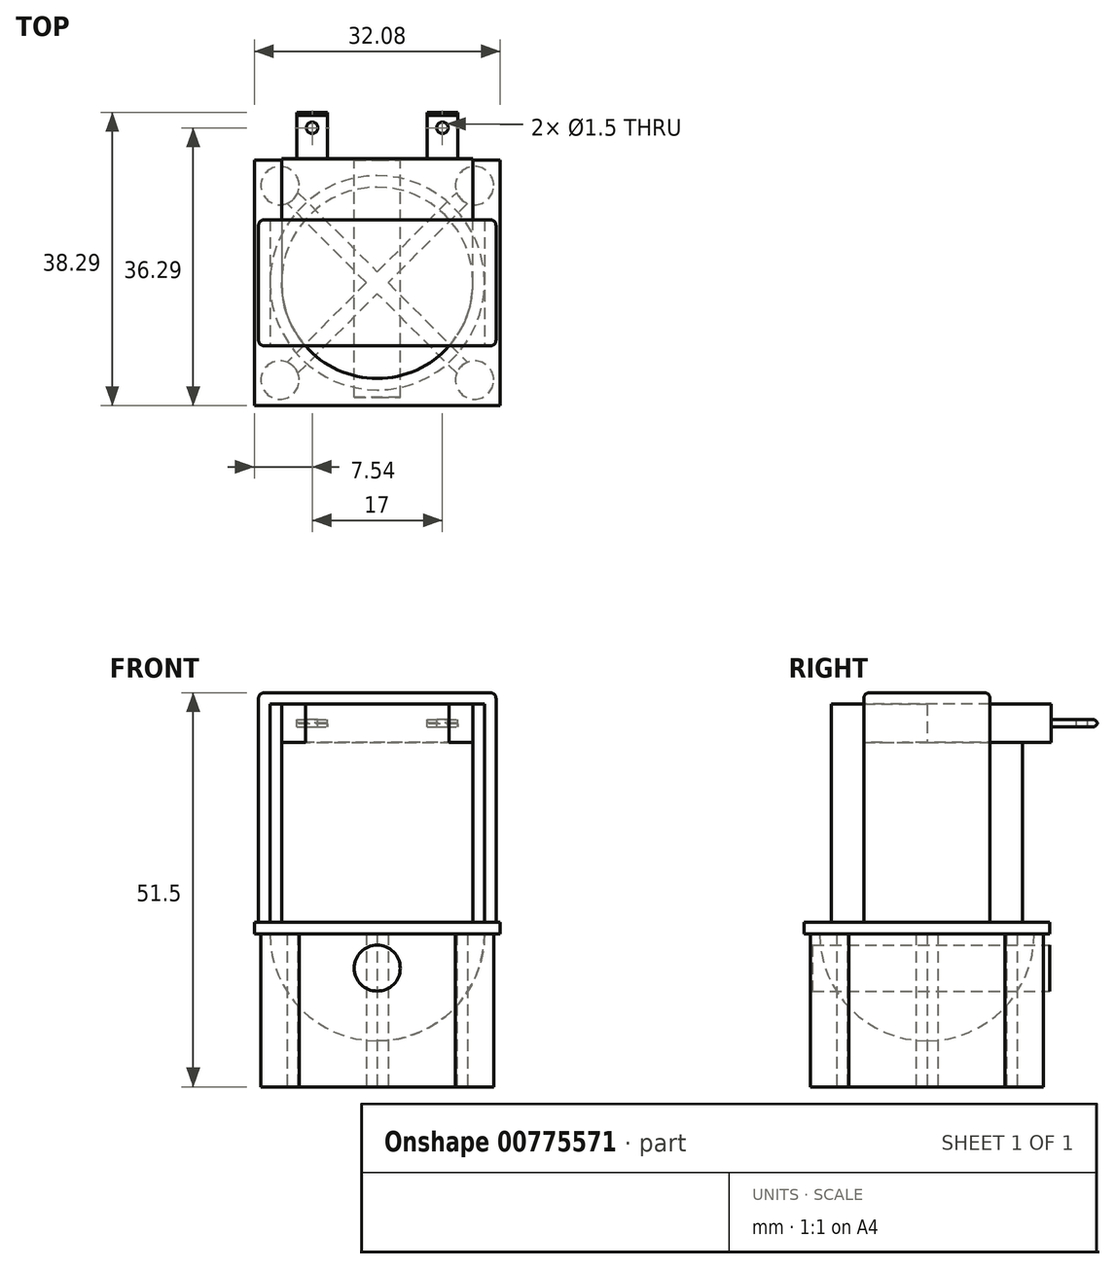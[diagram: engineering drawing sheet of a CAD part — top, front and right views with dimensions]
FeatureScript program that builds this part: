
annotation { "Feature Type Name" : "Feature", "Feature Type Description" : "" }
export const myFeature = defineFeature(function(context is Context, id is Id, definition is map)
    precondition{}
    {
        {
            var Q0;
            Q0=qCreatedBy(makeId("Top.planeOp"),FACE);
            var sketch = newSketch(context, id + "F0", { "sketchPlane" : qUnion([Q0])});
            skLineSegment(sketch, "E0.bottom", {"start": v(15.5, -8.25) * mm, "end": v(-15.5, -8.25) * mm});
            skLineSegment(sketch, "E0.top", {"start": v(15.5, 8.25) * mm, "end": v(-15.5, 8.25) * mm});
            skLineSegment(sketch, "E0.left", {"start": v(15.5, -8.25) * mm, "end": v(15.5, 8.25) * mm});
            skLineSegment(sketch, "E0.right", {"start": v(-15.5, -8.25) * mm, "end": v(-15.5, 8.25) * mm});
            skPoint(sketch, "E0.middle", {"position": v(0, 0) * mm});
            skSolve(sketch);
        }
        {
            var Q0;
            Q0 = qSketchRegion(id + "F0", true);
            extrude(context, id + "F1", {"entities" : qUnion([Q0]), "depth" : 30 * mm, "offsetDistance" : 25.4 * mm});
        }
        {
            var Q0;
            Q0=makeQuery(id+"F1.opExtrude","SWEPT_FACE",FACE,{"disambiguationData":[OSD([sQuery(id+"F0.wireOp",EDGE,"E0.bottom")])]});
            var sketch = newSketch(context, id + "F2", { "sketchPlane" : qUnion([Q0])});
            skLineSegment(sketch, "E1.bottom", {"start": v(-14, 0) * mm, "end": v(14, 0) * mm});
            skLineSegment(sketch, "E1.top", {"start": v(-14, 28.5) * mm, "end": v(14, 28.5) * mm});
            skLineSegment(sketch, "E1.left", {"start": v(-14, 0) * mm, "end": v(-14, 28.5) * mm});
            skLineSegment(sketch, "E1.right", {"start": v(14, 0) * mm, "end": v(14, 28.5) * mm});
            skSolve(sketch);
        }
        {
            var Q0;
            Q0 = qSketchRegion(id + "F2", true);
            extrude(context, id + "F3", {"entities" : qUnion([Q0]), "operationType" : NewBodyOperationType.REMOVE, "endBound" : BoundingType.UP_TO_NEXT, "oppositeDirection" : true, "depth" : 25.4 * mm, "offsetDistance" : 25.4 * mm});
        }
        {
            var Q0;
            Q0=makeQuery(id+"F1.opExtrude","SWEPT_EDGE",EDGE,{"disambiguationData":[OSD([sQuery(id+"F0.wireOp",EDGE,"E0.top"),sQuery(id+"F0.wireOp",EDGE,"E0.left")])]});
            var Q1;
            Q1=makeQuery(id+"F1.opExtrude","CAP_EDGE",EDGE,{"disambiguationData":[OSD([sQuery(id+"F0.wireOp",EDGE,"E0.top")])],"isStart":false});
            var Q2;
            Q2=makeQuery(id+"F1.opExtrude","SWEPT_EDGE",EDGE,{"disambiguationData":[OSD([sQuery(id+"F0.wireOp",EDGE,"E0.top"),sQuery(id+"F0.wireOp",EDGE,"E0.right")])]});
            var Q3;
            Q3=makeQuery(id+"F1.opExtrude","CAP_EDGE",EDGE,{"disambiguationData":[OSD([sQuery(id+"F0.wireOp",EDGE,"E0.left")])],"isStart":false});
            var Q4;
            Q4=makeQuery(id+"F1.opExtrude","SWEPT_EDGE",EDGE,{"disambiguationData":[OSD([sQuery(id+"F0.wireOp",EDGE,"E0.bottom"),sQuery(id+"F0.wireOp",EDGE,"E0.left")])]});
            var Q5;
            Q5=makeQuery(id+"F1.opExtrude","CAP_EDGE",EDGE,{"disambiguationData":[OSD([sQuery(id+"F0.wireOp",EDGE,"E0.bottom")])],"isStart":false});
            var Q6;
            Q6=makeQuery(id+"F1.opExtrude","CAP_EDGE",EDGE,{"disambiguationData":[OSD([sQuery(id+"F0.wireOp",EDGE,"E0.right")])],"isStart":false});
            var Q7;
            Q7=makeQuery(id+"F1.opExtrude","SWEPT_EDGE",EDGE,{"disambiguationData":[OSD([sQuery(id+"F0.wireOp",EDGE,"E0.bottom"),sQuery(id+"F0.wireOp",EDGE,"E0.right")])]});
            fillet(context, id + "F4", {"entities" : qUnion([Q0, Q1, Q2, Q3, Q4, Q5, Q6, Q7]), "radius" : 0.76 * mm, "tangentPropagation" : true, "allowEdgeOverflow" : false});
        }
        {
            var Q0;
            Q0=makeQuery(id+"F3.boolean.opBoolean","COPY",FACE,{"derivedFrom":makeQuery(id+"F3.opExtrude","SWEPT_FACE",FACE,{"disambiguationData":[OSD([sQuery(id+"F2.wireOp",EDGE,"E1.top")])]})});
            var sketch = newSketch(context, id + "F5", { "sketchPlane" : qUnion([Q0])});
            skLineSegment(sketch, "E2.bottom", {"start": v(14, -16.25) * mm, "end": v(-14, -16.25) * mm});
            skLineSegment(sketch, "E2.top", {"start": v(14, 8.25) * mm, "end": v(-14, 8.25) * mm});
            skLineSegment(sketch, "E2.left", {"start": v(14, -16.25) * mm, "end": v(14, 8.25) * mm});
            skLineSegment(sketch, "E2.right", {"start": v(-14, -16.25) * mm, "end": v(-14, 8.25) * mm});
            skSolve(sketch);
        }
        {
            var Q0;
            Q0 = qSketchRegion(id + "F5", true);
            extrude(context, id + "F6", {"entities" : qUnion([Q0]), "operationType" : NewBodyOperationType.ADD, "depth" : 5 * mm, "offsetDistance" : 25.4 * mm});
        }
        {
            var Q0;
            Q0=makeQuery(id+"F6.opExtrude","CAP_FACE",FACE,{"disambiguationData":[OSD([sQuery(id+"F5.wireOp",EDGE,"E2.bottom"),sQuery(id+"F5.wireOp",EDGE,"E2.top"),sQuery(id+"F5.wireOp",EDGE,"E2.left"),sQuery(id+"F5.wireOp",EDGE,"E2.right")])],"isStart":false});
            var sketch = newSketch(context, id + "F7", { "sketchPlane" : qUnion([Q0])});
            skCircle(sketch, "E3", {"center": v(0, 0) * mm, "radius": 12.5 * mm});
            skSolve(sketch);
        }
        {
            var Q0;
            Q0 = qSketchRegion(id + "F7", true);
            extrude(context, id + "F8", {"entities" : qUnion([Q0]), "operationType" : NewBodyOperationType.ADD, "depth" : 30 * mm - 6.5 * mm, "offsetDistance" : 25.4 * mm});
        }
        {
            var Q0;
            Q0=makeQuery(id+"F6.opExtrude","CAP_FACE",FACE,{"disambiguationData":[OSD([sQuery(id+"F5.wireOp",EDGE,"E2.bottom"),sQuery(id+"F5.wireOp",EDGE,"E2.top"),sQuery(id+"F5.wireOp",EDGE,"E2.left"),sQuery(id+"F5.wireOp",EDGE,"E2.right")])],"isStart":false});
            var sketch = newSketch(context, id + "F9", { "sketchPlane" : qUnion([Q0])});
            skLineSegment(sketch, "E4", {"start": v(12.5, 0) * mm, "end": v(12.5, -16.25) * mm});
            skLineSegment(sketch, "E5", {"start": v(12.5, -16.25) * mm, "end": v(14, -16.25) * mm});
            skLineSegment(sketch, "E6", {"start": v(14, -16.25) * mm, "end": v(14, 8.25) * mm});
            skLineSegment(sketch, "E7", {"start": v(14, 8.25) * mm, "end": v(9.4, 8.25) * mm});
            skFitSpline(sketch, "E8", {"points": [v(9.4, 8.25) * mm, v(11.08, 5.78) * mm, v(12.08, 3.2) * mm, v(12.5, 0) * mm], "startDerivative": vector(5.27, -6.62) * mm, "endDerivative": vector(0.18, -6.77) * mm});
            skFitSpline(sketch, "E9", {"points": [v(-9.4, 8.25) * mm, v(-10.86, 6.2) * mm, v(-12.05, 3.31) * mm, v(-12.5, 0) * mm], "startDerivative": vector(-4.94, -6.33) * mm, "endDerivative": vector(-0.79, -9.5) * mm});
            skLineSegment(sketch, "E10", {"start": v(-9.4, 8.25) * mm, "end": v(-14, 8.25) * mm});
            skLineSegment(sketch, "E11", {"start": v(-14, 8.25) * mm, "end": v(-14, -16.25) * mm});
            skLineSegment(sketch, "E12", {"start": v(-14, -16.25) * mm, "end": v(-12.5, -16.25) * mm});
            skLineSegment(sketch, "E13", {"start": v(-12.5, -16.25) * mm, "end": v(-12.5, 0) * mm});
            skSolve(sketch);
        }
        {
            var Q0;
            Q0 = qSketchRegion(id + "F9", true);
            extrude(context, id + "F10", {"entities" : qUnion([Q0]), "operationType" : NewBodyOperationType.REMOVE, "oppositeDirection" : true, "depth" : 5 * mm, "offsetDistance" : 25.4 * mm});
        }
        {
            var Q0;
            Q0=makeQuery(id+"F6.opExtrude","SWEPT_FACE",FACE,{"disambiguationData":[OSD([sQuery(id+"F5.wireOp",EDGE,"E2.bottom")])]});
            var sketch = newSketch(context, id + "F11", { "sketchPlane" : qUnion([Q0])});
            skLineSegment(sketch, "E14.bottom", {"start": v(10.5, 25.5) * mm, "end": v(6.5, 25.5) * mm});
            skLineSegment(sketch, "E14.top", {"start": v(10.5, 26.5) * mm, "end": v(6.5, 26.5) * mm});
            skLineSegment(sketch, "E14.left", {"start": v(10.5, 25.5) * mm, "end": v(10.5, 26.5) * mm});
            skLineSegment(sketch, "E14.right", {"start": v(6.5, 25.5) * mm, "end": v(6.5, 26.5) * mm});
            skLineSegment(sketch, "E15.bottom", {"start": v(-6.5, 25.5) * mm, "end": v(-10.5, 25.5) * mm});
            skLineSegment(sketch, "E15.top", {"start": v(-6.5, 26.5) * mm, "end": v(-10.5, 26.5) * mm});
            skLineSegment(sketch, "E15.left", {"start": v(-6.5, 25.5) * mm, "end": v(-6.5, 26.5) * mm});
            skLineSegment(sketch, "E15.right", {"start": v(-10.5, 25.5) * mm, "end": v(-10.5, 26.5) * mm});
            skLineSegment(sketch, "E16", {"start": v(0, 28.5) * mm, "end": v(0, 23.5) * mm});
            skLineSegment(sketch, "E17", {"start": v(-12.5, 26) * mm, "end": v(12.5, 26) * mm});
            skLineSegment(sketch, "E18", {"start": v(-8.5, 26.5) * mm, "end": v(-8.5, 25.5) * mm});
            skLineSegment(sketch, "E19", {"start": v(8.5, 26.5) * mm, "end": v(8.5, 25.5) * mm});
            skSolve(sketch);
        }
        {
            var Q0;
            Q0 = qSketchRegion(id + "F11", true);
            extrude(context, id + "F12", {"entities" : qUnion([Q0]), "operationType" : NewBodyOperationType.ADD, "depth" : 6 * mm, "offsetDistance" : 25.4 * mm});
        }
        {
            var Q0;
            Q0=makeQuery(id+"F12.opExtrude","SWEPT_FACE",FACE,{"disambiguationData":[OSD([sQuery(id+"F11.wireOp",EDGE,"E15.top")])]});
            var sketch = newSketch(context, id + "F13", { "sketchPlane" : qUnion([Q0])});
            skCircle(sketch, "E20", {"center": v(8.5, 20.25) * mm, "radius": 0.75 * mm});
            skCircle(sketch, "E21", {"center": v(-8.5, 20.25) * mm, "radius": 0.75 * mm});
            skSolve(sketch);
        }
        {
            var Q0;
            Q0 = qSketchRegion(id + "F13", true);
            extrude(context, id + "F14", {"entities" : qUnion([Q0]), "operationType" : NewBodyOperationType.REMOVE, "endBound" : BoundingType.UP_TO_NEXT, "oppositeDirection" : true, "depth" : 25.4 * mm, "offsetDistance" : 25.4 * mm});
        }
        {
            var Q0;
            Q0=makeQuery(id+"F12.opExtrude","CAP_EDGE",EDGE,{"disambiguationData":[OSD([sQuery(id+"F11.wireOp",EDGE,"E15.top")])],"isStart":false});
            var Q1;
            Q1=makeQuery(id+"F12.opExtrude","CAP_EDGE",EDGE,{"disambiguationData":[OSD([sQuery(id+"F11.wireOp",EDGE,"E14.top")])],"isStart":false});
            chamfer(context, id + "F15", {"entities" : qUnion([Q0, Q1]), "width" : 0.4 * mm, "tangentPropagation" : true});
        }
        {
            var Q0;
            Q0=makeQuery(id+"F12.opExtrude","CAP_EDGE",EDGE,{"disambiguationData":[OSD([sQuery(id+"F11.wireOp",EDGE,"E15.bottom")])],"isStart":false});
            var Q1;
            Q1=makeQuery(id+"F12.opExtrude","CAP_EDGE",EDGE,{"disambiguationData":[OSD([sQuery(id+"F11.wireOp",EDGE,"E14.bottom")])],"isStart":false});
            chamfer(context, id + "F16", {"entities" : qUnion([Q0, Q1]), "width" : 0.4 * mm, "tangentPropagation" : true});
        }
        {
            var Q0;
            Q0=makeQuery(id+"F8.opExtrude","CAP_FACE",FACE,{"disambiguationData":[OSD([sQuery(id+"F7.wireOp",EDGE,"E3")])],"isStart":true});
            var sketch = newSketch(context, id + "F17", { "sketchPlane" : qUnion([Q0])});
            skArc(sketch, "E22", {"start": v(-9.4, -8.25) * mm, "mid": v(0, -12.5) * mm, "end": v(9.4, -8.25) * mm});
            skLineSegment(sketch, "E23", {"start": v(9.4, -8.25) * mm, "end": v(-9.4, -8.25) * mm});
            skSolve(sketch);
        }
        {
            var Q0;
            Q0 = qSketchRegion(id + "F17", true);
            extrude(context, id + "F18", {"entities" : qUnion([Q0]), "operationType" : NewBodyOperationType.ADD, "depth" : 5 * mm, "offsetDistance" : 25.4 * mm});
        }
        {
            var Q0;
            Q0=makeQuery(id+"F8.opExtrude","CAP_FACE",FACE,{"disambiguationData":[OSD([sQuery(id+"F7.wireOp",EDGE,"E3")])],"isStart":false});
            var sketch = newSketch(context, id + "F19", { "sketchPlane" : qUnion([Q0])});
            skLineSegment(sketch, "E24.bottom", {"start": v(16.04, -16.04) * mm, "end": v(-16.04, -16.04) * mm});
            skLineSegment(sketch, "E24.top", {"start": v(16.04, 16.04) * mm, "end": v(-16.04, 16.04) * mm});
            skLineSegment(sketch, "E24.left", {"start": v(16.04, -16.04) * mm, "end": v(16.04, 16.04) * mm});
            skLineSegment(sketch, "E24.right", {"start": v(-16.04, -16.04) * mm, "end": v(-16.04, 16.04) * mm});
            skPoint(sketch, "E24.middle", {"position": v(0, 0) * mm});
            skSolve(sketch);
        }
        {
            var Q0;
            Q0 = qSketchRegion(id + "F19", true);
            extrude(context, id + "F20", {"entities" : qUnion([Q0]), "operationType" : NewBodyOperationType.ADD, "depth" : 1.5 * mm, "offsetDistance" : 25.4 * mm});
        }
        {
            var Q0;
            Q0=makeQuery(id+"F20.opExtrude","CAP_FACE",FACE,{"disambiguationData":[OSD([sQuery(id+"F19.wireOp",EDGE,"E24.bottom"),sQuery(id+"F19.wireOp",EDGE,"E24.top"),sQuery(id+"F19.wireOp",EDGE,"E24.left"),sQuery(id+"F19.wireOp",EDGE,"E24.right")])],"isStart":false});
            var sketch = newSketch(context, id + "F21", { "sketchPlane" : qUnion([Q0])});
            skCircle(sketch, "E25", {"center": v(12.7, 12.7) * mm, "radius": 2.5 * mm});
            skCircle(sketch, "E26", {"center": v(12.7, -12.7) * mm, "radius": 2.5 * mm});
            skCircle(sketch, "E27", {"center": v(-12.7, -12.7) * mm, "radius": 2.5 * mm});
            skCircle(sketch, "E28", {"center": v(-12.7, 12.7) * mm, "radius": 2.5 * mm});
            skLineSegment(sketch, "E29", {"start": v(-12.7, 10.2) * mm, "end": v(-12.7, -10.2) * mm});
            skLineSegment(sketch, "E30", {"start": v(-10.2, -12.7) * mm, "end": v(10.2, -12.7) * mm});
            skLineSegment(sketch, "E31", {"start": v(12.7, -10.2) * mm, "end": v(12.7, 10.2) * mm});
            skLineSegment(sketch, "E32", {"start": v(10.2, 12.7) * mm, "end": v(-10.2, 12.7) * mm});
            skSolve(sketch);
        }
        {
            var Q0;
            {var subQ0=sQuery(id+"F21.wireOp",EDGE,"E27");var subQ1=makeQuery(id+"F21.imprint","INTERSECT",VERTEX,{"derivedFrom":[subQ0,sQuery(id+"F21.wireOp",EDGE,"E29")]});Q0=makeQuery(id+"F21.imprint","IMPRINT",FACE,{"disambiguationData":[TD([[makeQuery(id+"F21.imprint","IMPRINT",EDGE,{"disambiguationData":[TD([[subQ1,1.0]])],"derivedFrom":subQ0}),1.0]])]});}
            var Q1;
            {var subQ0=sQuery(id+"F21.wireOp",EDGE,"E28");var subQ1=makeQuery(id+"F21.imprint","INTERSECT",VERTEX,{"derivedFrom":[subQ0,sQuery(id+"F21.wireOp",EDGE,"E29")]});Q1=makeQuery(id+"F21.imprint","IMPRINT",FACE,{"disambiguationData":[TD([[makeQuery(id+"F21.imprint","IMPRINT",EDGE,{"disambiguationData":[TD([[subQ1,1.0]])],"derivedFrom":subQ0}),1.0]])]});}
            var Q2;
            {var subQ0=sQuery(id+"F21.wireOp",EDGE,"E25");var subQ1=makeQuery(id+"F21.imprint","INTERSECT",VERTEX,{"derivedFrom":[subQ0,sQuery(id+"F21.wireOp",EDGE,"E31")]});Q2=makeQuery(id+"F21.imprint","IMPRINT",FACE,{"disambiguationData":[TD([[makeQuery(id+"F21.imprint","IMPRINT",EDGE,{"disambiguationData":[TD([[subQ1,1.0]])],"derivedFrom":subQ0}),1.0]])]});}
            var Q3;
            {var subQ0=sQuery(id+"F21.wireOp",EDGE,"E26");var subQ1=makeQuery(id+"F21.imprint","INTERSECT",VERTEX,{"derivedFrom":[subQ0,sQuery(id+"F21.wireOp",EDGE,"E30")]});Q3=makeQuery(id+"F21.imprint","IMPRINT",FACE,{"disambiguationData":[TD([[makeQuery(id+"F21.imprint","IMPRINT",EDGE,{"disambiguationData":[TD([[subQ1,1.0]])],"derivedFrom":subQ0}),1.0]])]});}
            extrude(context, id + "F22", {"entities" : qUnion([Q0, Q1, Q2, Q3]), "operationType" : NewBodyOperationType.ADD, "depth" : 20 * mm, "offsetDistance" : 25.4 * mm});
        }
        {
            var Q0;
            Q0=qCreatedBy(makeId("Front.planeOp"),FACE);
            var sketch = newSketch(context, id + "F23", { "sketchPlane" : qUnion([Q0])});
            skLineSegment(sketch, "E33", {"start": v(0, 0) * mm, "end": v(14, 0) * mm});
            skLineSegment(sketch, "E34", {"start": v(14, 0) * mm, "end": v(14, -1.5) * mm});
            skLineSegment(sketch, "E35", {"start": v(0, 0) * mm, "end": v(-14, 0) * mm});
            skLineSegment(sketch, "E36", {"start": v(-14, 0) * mm, "end": v(-14, -1.5) * mm});
            skArc(sketch, "E37", {"start": v(-14, -1.5) * mm, "mid": v(0, -15.5) * mm, "end": v(14, -1.5) * mm});
            skLineSegment(sketch, "E38", {"start": v(0, -17.2) * mm, "end": v(0, 0) * mm});
            skSolve(sketch);
        }
        {
            var Q0;
            Q0=makeQuery(id+"F23.imprint","IMPRINT",FACE,{"disambiguationData":[TD([[makeQuery(id+"F23.imprint","IMPRINT",EDGE,{"derivedFrom":sQuery(id+"F23.wireOp",EDGE,"E33")}),-1.0]])]});
            var Q1;
            Q1=sQuery(id+"F23.wireOp",EDGE,"E38");
            revolve(context, id + "F24", {"operationType" : NewBodyOperationType.ADD, "surfaceOperationType" : NewSurfaceOperationType.NEW, "entities" : qUnion([Q0]), "axis" : qUnion([Q1]), "revolveType" : RevolveType.FULL});
        }
        {
            var Q0;
            Q0=makeQuery(id+"F22.opExtrude","CAP_FACE",FACE,{"disambiguationData":[OSD([sQuery(id+"F21.wireOp",EDGE,"E27")])],"isStart":false});
            var sketch = newSketch(context, id + "F25", { "sketchPlane" : qUnion([Q0])});
            skLineSegment(sketch, "E39", {"start": v(-10.37, -11.8) * mm, "end": v(11.77, 10.38) * mm});
            skLineSegment(sketch, "E40", {"start": v(10.37, 11.8) * mm, "end": v(-11.77, -10.38) * mm});
            skArc(sketch, "E41", {"start": v(-10.37, -11.8) * mm, "mid": v(-10.92, -10.95) * mm, "end": v(-11.77, -10.38) * mm});
            skArc(sketch, "E42", {"start": v(10.37, 11.8) * mm, "mid": v(10.92, 10.95) * mm, "end": v(11.77, 10.38) * mm});
            skLineSegment(sketch, "E43", {"start": v(0, -1.42) * mm, "end": v(10.37, -11.8) * mm});
            skLineSegment(sketch, "E44", {"start": v(11.77, -10.38) * mm, "end": v(1.41, 0) * mm});
            skLineSegment(sketch, "E45", {"start": v(-1.41, 0) * mm, "end": v(-11.77, 10.38) * mm});
            skLineSegment(sketch, "E46", {"start": v(-10.37, 11.8) * mm, "end": v(0, 1.42) * mm});
            skArc(sketch, "E47", {"start": v(-11.77, 10.38) * mm, "mid": v(-10.92, 10.94) * mm, "end": v(-10.37, 11.8) * mm});
            skArc(sketch, "E48", {"start": v(11.77, -10.38) * mm, "mid": v(10.92, -10.94) * mm, "end": v(10.37, -11.8) * mm});
            skSolve(sketch);
        }
        {
            var Q0;
            Q0 = qSketchRegion(id + "F25", true);
            extrude(context, id + "F26", {"entities" : qUnion([Q0]), "oppositeDirection" : true, "depth" : 20 * mm, "offsetDistance" : 25.4 * mm});
        }
        {
            var Q0;
            Q0=makeQuery(id+"F20.opExtrude","SWEPT_FACE",FACE,{"disambiguationData":[OSD([sQuery(id+"F19.wireOp",EDGE,"E24.bottom")])]});
            var sketch = newSketch(context, id + "F27", { "sketchPlane" : qUnion([Q0])});
            skCircle(sketch, "E49", {"center": v(0, -6) * mm, "radius": 3 * mm});
            skSolve(sketch);
        }
        {
            var Q0;
            Q0 = qSketchRegion(id + "F27", true);
            extrude(context, id + "F28", {"entities" : qUnion([Q0]), "oppositeDirection" : true, "depth" : 31 * mm, "offsetDistance" : 25.4 * mm});
        }
    });
